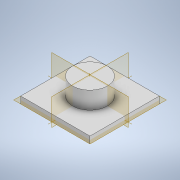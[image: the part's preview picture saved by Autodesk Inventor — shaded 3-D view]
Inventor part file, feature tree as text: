
AUTODESK INVENTOR PART (.ipt)
format: ipt  version: 2022.4 (Build 264492010, 492A)  size: 108,544 bytes
history: native  units: mm
features: extrude x2, sketch x2
ambient origin geometry x8: Origin, YZ Plane, XZ Plane, XY Plane, X Axis, Y Axis, Z Axis, Center Point
bodies: Solid1 (feature_tree)
feature tree (4):
  extrude  "Extrusion1"  Depth=10.0mm
  extrude  "Extrusion2"  Depth=2.5mm
  sketch  "Sketch1"  dims[d0=10.0mm d1=10.0mm]
  sketch  "Sketch2"  dims[d2=1.0mm d3=0.0mm d4=5.0mm d5=2.5mm d6=0.0mm]
